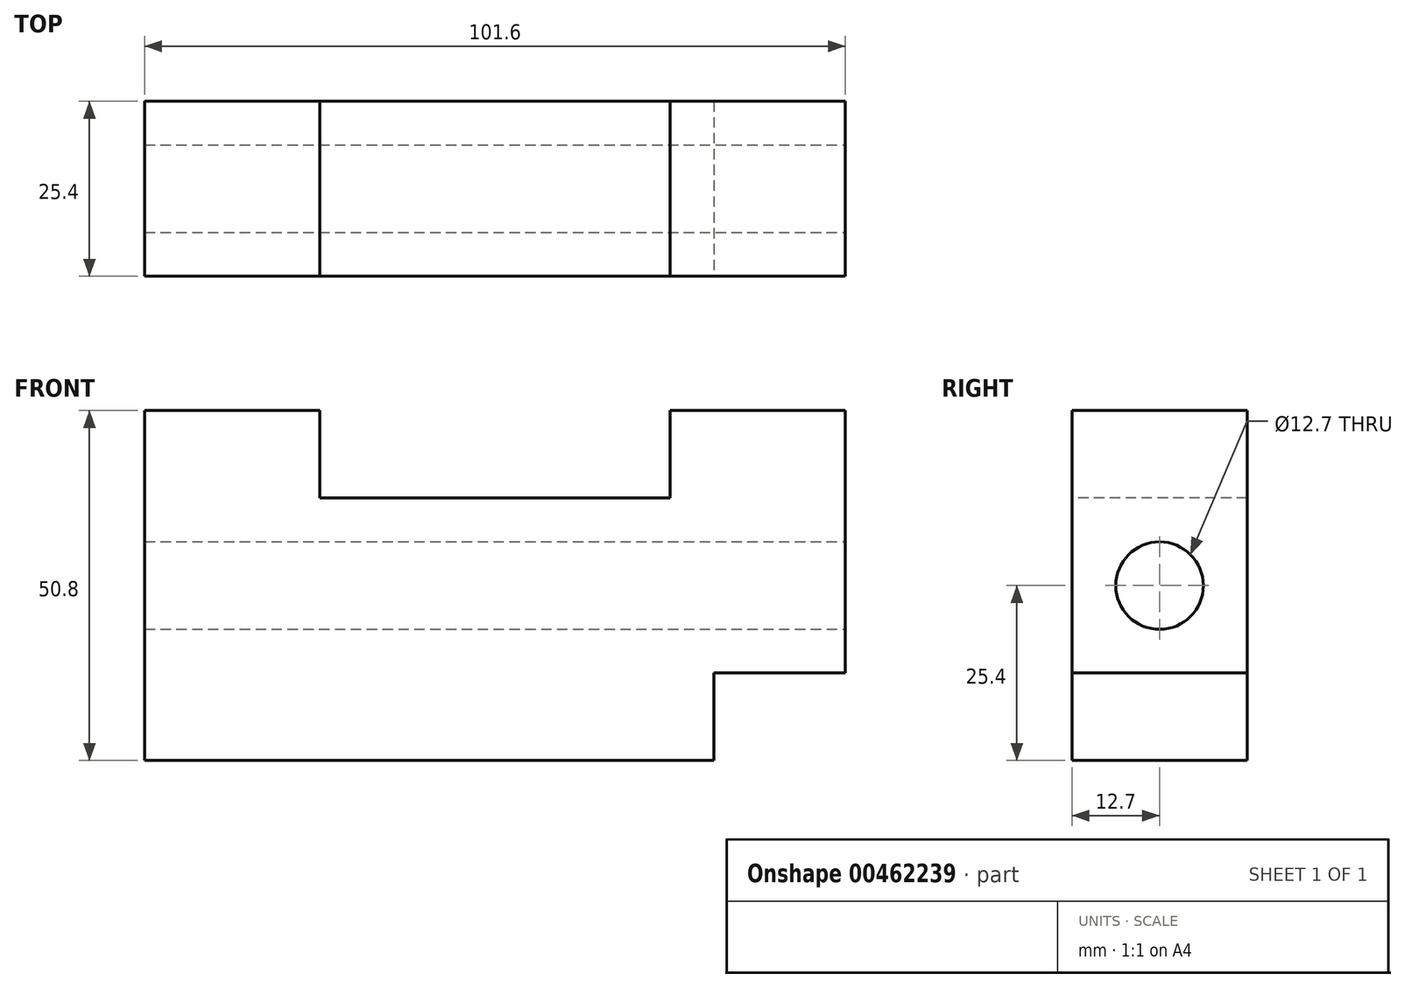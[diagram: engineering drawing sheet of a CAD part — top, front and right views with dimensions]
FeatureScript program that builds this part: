
annotation { "Feature Type Name" : "Feature", "Feature Type Description" : "" }
export const myFeature = defineFeature(function(context is Context, id is Id, definition is map)
    precondition{}
    {
        {
            var Q0;
            Q0=qCreatedBy(makeId("Front.planeOp"),FACE);
            var sketch = newSketch(context, id + "F0", { "sketchPlane" : qUnion([Q0])});
            skLineSegment(sketch, "E0.bottom", {"start": v(50.8, 25.4) * mm, "end": v(-50.8, 25.4) * mm});
            skLineSegment(sketch, "E0.top", {"start": v(50.8, -25.4) * mm, "end": v(-50.8, -25.4) * mm});
            skLineSegment(sketch, "E0.left", {"start": v(50.8, 25.4) * mm, "end": v(50.8, -25.4) * mm});
            skLineSegment(sketch, "E0.right", {"start": v(-50.8, 25.4) * mm, "end": v(-50.8, -25.4) * mm});
            skPoint(sketch, "E0.middle", {"position": v(0, 0) * mm});
            skSolve(sketch);
        }
        {
            var Q0;
            Q0 = qSketchRegion(id + "F0", true);
            extrude(context, id + "F1", {"entities" : qUnion([Q0]), "depth" : 25.4 * mm});
        }
        {
            var Q0;
            Q0=makeQuery(id+"F1.opExtrude","CAP_FACE",FACE,{"disambiguationData":[OSD([sQuery(id+"F0.wireOp",EDGE,"E0.bottom"),sQuery(id+"F0.wireOp",EDGE,"E0.top"),sQuery(id+"F0.wireOp",EDGE,"E0.left"),sQuery(id+"F0.wireOp",EDGE,"E0.right")])],"isStart":false});
            var sketch = newSketch(context, id + "F2", { "sketchPlane" : qUnion([Q0])});
            skLineSegment(sketch, "E1.bottom", {"start": v(50.8, -25.4) * mm, "end": v(31.75, -25.4) * mm});
            skLineSegment(sketch, "E1.top", {"start": v(50.8, -12.7) * mm, "end": v(31.75, -12.7) * mm});
            skLineSegment(sketch, "E1.left", {"start": v(50.8, -25.4) * mm, "end": v(50.8, -12.7) * mm});
            skLineSegment(sketch, "E1.right", {"start": v(31.75, -25.4) * mm, "end": v(31.75, -12.7) * mm});
            skSolve(sketch);
        }
        {
            var Q0;
            Q0=makeQuery(id+"F2.imprint","IMPRINT",FACE,{"disambiguationData":[TD([[makeQuery(id+"F2.imprint","IMPRINT",EDGE,{"derivedFrom":sQuery(id+"F2.wireOp",EDGE,"E1.bottom")}),-1.0]])]});
            extrude(context, id + "F3", {"entities" : qUnion([Q0]), "operationType" : NewBodyOperationType.REMOVE, "oppositeDirection" : true, "depth" : 25.4 * mm});
        }
        {
            var Q0;
            Q0=makeQuery(id+"F1.opExtrude","CAP_FACE",FACE,{"disambiguationData":[OSD([sQuery(id+"F0.wireOp",EDGE,"E0.bottom"),sQuery(id+"F0.wireOp",EDGE,"E0.top"),sQuery(id+"F0.wireOp",EDGE,"E0.left"),sQuery(id+"F0.wireOp",EDGE,"E0.right")])],"isStart":false});
            var sketch = newSketch(context, id + "F4", { "sketchPlane" : qUnion([Q0])});
            skLineSegment(sketch, "E2.bottom", {"start": v(-25.4, 25.4) * mm, "end": v(25.4, 25.4) * mm});
            skLineSegment(sketch, "E2.top", {"start": v(-25.4, 12.7) * mm, "end": v(25.4, 12.7) * mm});
            skLineSegment(sketch, "E2.left", {"start": v(-25.4, 25.4) * mm, "end": v(-25.4, 12.7) * mm});
            skLineSegment(sketch, "E2.right", {"start": v(25.4, 25.4) * mm, "end": v(25.4, 12.7) * mm});
            skSolve(sketch);
        }
        {
            var Q0;
            Q0=makeQuery(id+"F4.imprint","IMPRINT",FACE,{"disambiguationData":[TD([[makeQuery(id+"F4.imprint","IMPRINT",EDGE,{"derivedFrom":sQuery(id+"F4.wireOp",EDGE,"E2.bottom")}),1.0]])]});
            extrude(context, id + "F5", {"entities" : qUnion([Q0]), "operationType" : NewBodyOperationType.REMOVE, "oppositeDirection" : true, "depth" : 25.4 * mm});
        }
        {
            var Q0;
            Q0=makeQuery(id+"F1.opExtrude","SWEPT_FACE",FACE,{"disambiguationData":[OSD([sQuery(id+"F0.wireOp",EDGE,"E0.left")])]});
            var sketch = newSketch(context, id + "F6", { "sketchPlane" : qUnion([Q0])});
            skCircle(sketch, "E3", {"center": v(-12.7, 0) * mm, "radius": 6.35 * mm});
            skSolve(sketch);
        }
        {
            var Q0;
            Q0=makeQuery(id+"F6.imprint","IMPRINT",FACE,{"disambiguationData":[TD([[makeQuery(id+"F6.imprint","IMPRINT",EDGE,{"derivedFrom":sQuery(id+"F6.wireOp",EDGE,"E3")}),1.0]])]});
            extrude(context, id + "F7", {"entities" : qUnion([Q0]), "operationType" : NewBodyOperationType.REMOVE, "oppositeDirection" : true, "depth" : 101.6 * mm});
        }
    });
